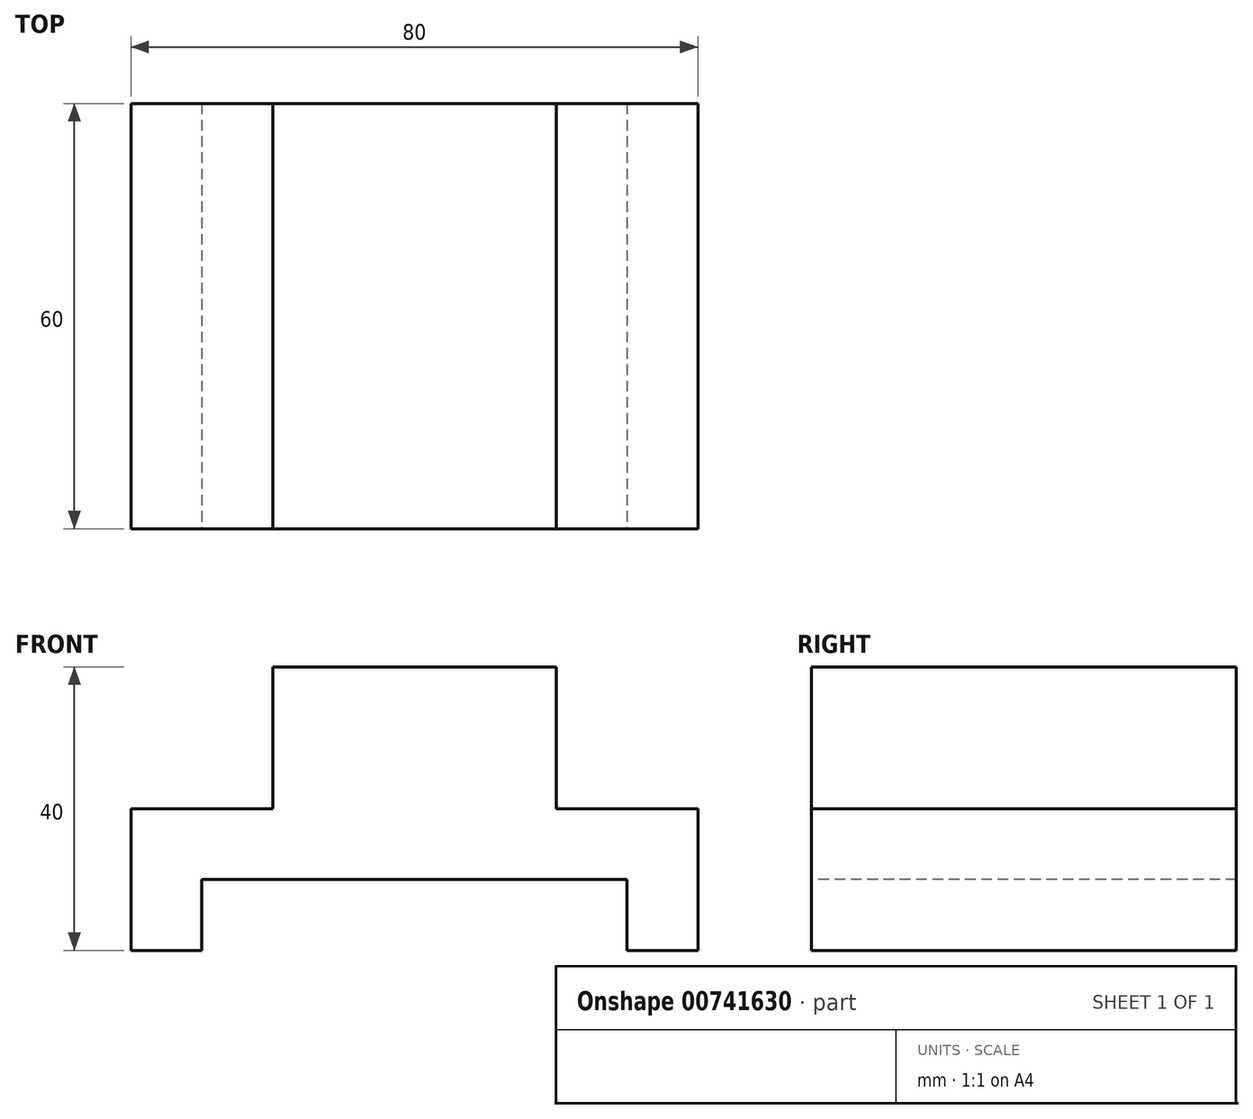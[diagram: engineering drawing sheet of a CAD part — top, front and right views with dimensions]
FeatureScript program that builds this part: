
annotation { "Feature Type Name" : "Feature", "Feature Type Description" : "" }
export const myFeature = defineFeature(function(context is Context, id is Id, definition is map)
    precondition{}
    {
        {
            var Q0;
            Q0=qCreatedBy(makeId("Front.planeOp"),FACE);
            var sketch = newSketch(context, id + "F0", { "sketchPlane" : qUnion([Q0])});
            skLineSegment(sketch, "E0.bottom", {"start": v(-40, -20) * mm, "end": v(40, -20) * mm});
            skLineSegment(sketch, "E0.top", {"start": v(-40, 20) * mm, "end": v(40, 20) * mm});
            skLineSegment(sketch, "E0.left", {"start": v(-40, -20) * mm, "end": v(-40, 20) * mm});
            skLineSegment(sketch, "E0.right", {"start": v(40, -20) * mm, "end": v(40, 20) * mm});
            skPoint(sketch, "E0.middle", {"position": v(0, 0) * mm});
            skSolve(sketch);
        }
        {
            var Q0;
            Q0=makeQuery(id+"F0.imprint","IMPRINT",FACE,{"disambiguationData":[TD([[makeQuery(id+"F0.imprint","IMPRINT",EDGE,{"derivedFrom":sQuery(id+"F0.wireOp",EDGE,"E0.bottom")}),1.0]])]});
            extrude(context, id + "F1", {"entities" : qUnion([Q0]), "depth" : 60 * mm, "offsetDistance" : 25.4 * mm});
        }
        {
            var Q0;
            Q0=makeQuery(id+"F1.opExtrude","CAP_FACE",FACE,{"disambiguationData":[OSD([sQuery(id+"F0.wireOp",EDGE,"E0.bottom"),sQuery(id+"F0.wireOp",EDGE,"E0.top"),sQuery(id+"F0.wireOp",EDGE,"E0.left"),sQuery(id+"F0.wireOp",EDGE,"E0.right")])],"isStart":false});
            var sketch = newSketch(context, id + "F2", { "sketchPlane" : qUnion([Q0])});
            skLineSegment(sketch, "E1", {"start": v(-20, 20) * mm, "end": v(-20, 0) * mm});
            skLineSegment(sketch, "E2", {"start": v(-20, 0) * mm, "end": v(-40, 0) * mm});
            skLineSegment(sketch, "E3", {"start": v(-40, 0) * mm, "end": v(-40, 20) * mm});
            skLineSegment(sketch, "E4", {"start": v(-40, 20) * mm, "end": v(-20, 20) * mm});
            skLineSegment(sketch, "E5", {"start": v(20, 20) * mm, "end": v(20, 0) * mm});
            skLineSegment(sketch, "E6", {"start": v(20, 0) * mm, "end": v(40, 0) * mm});
            skLineSegment(sketch, "E7", {"start": v(40, 0) * mm, "end": v(40, 20) * mm});
            skLineSegment(sketch, "E8", {"start": v(40, 20) * mm, "end": v(20, 20) * mm});
            skLineSegment(sketch, "E9.bottom", {"start": v(-30, -20) * mm, "end": v(30, -20) * mm});
            skLineSegment(sketch, "E9.top", {"start": v(-30, -10) * mm, "end": v(30, -10) * mm});
            skLineSegment(sketch, "E9.left", {"start": v(-30, -20) * mm, "end": v(-30, -10) * mm});
            skLineSegment(sketch, "E9.right", {"start": v(30, -20) * mm, "end": v(30, -10) * mm});
            skSolve(sketch);
        }
        {
            var Q0;
            Q0=makeQuery(id+"F2.imprint","IMPRINT",FACE,{"disambiguationData":[TD([[makeQuery(id+"F2.imprint","IMPRINT",EDGE,{"derivedFrom":sQuery(id+"F2.wireOp",EDGE,"E5")}),1.0]])]});
            var Q1;
            Q1=makeQuery(id+"F2.imprint","IMPRINT",FACE,{"disambiguationData":[TD([[makeQuery(id+"F2.imprint","IMPRINT",EDGE,{"derivedFrom":sQuery(id+"F2.wireOp",EDGE,"E1")}),-1.0]])]});
            extrude(context, id + "F3", {"entities" : qUnion([Q0, Q1]), "operationType" : NewBodyOperationType.REMOVE, "endBound" : BoundingType.THROUGH_ALL, "oppositeDirection" : true, "depth" : 25.4 * mm, "offsetDistance" : 25.4 * mm});
        }
        {
            var Q0;
            Q0=makeQuery(id+"F2.imprint","IMPRINT",FACE,{"disambiguationData":[TD([[makeQuery(id+"F2.imprint","IMPRINT",EDGE,{"derivedFrom":sQuery(id+"F2.wireOp",EDGE,"E9.bottom")}),1.0]])]});
            extrude(context, id + "F4", {"entities" : qUnion([Q0]), "operationType" : NewBodyOperationType.REMOVE, "endBound" : BoundingType.THROUGH_ALL, "oppositeDirection" : true, "depth" : 25.4 * mm, "offsetDistance" : 25.4 * mm});
        }
    });
